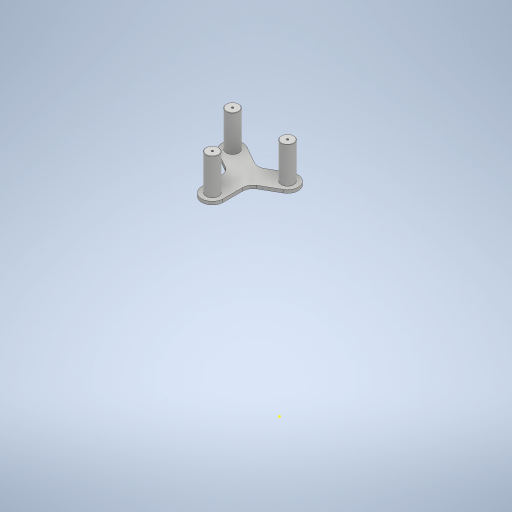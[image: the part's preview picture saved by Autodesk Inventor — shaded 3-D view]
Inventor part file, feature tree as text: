
AUTODESK INVENTOR PART (.ipt)
format: ipt  version: 2023 (Build 270158000, 158)  size: 315,904 bytes
history: native  units: mm
features: extrude x3, sketch x3, hole x3, plane x2, fillet x1
ambient origin geometry x8: Origin, YZ Plane, XZ Plane, XY Plane, X Axis, Y Axis, Z Axis, Center Point
bodies: 实体1 (feature_tree)
feature tree (12):
  plane  "工作平面5"
  extrude  "拉伸1"  Depth=12.0mm
  plane  "工作平面2"
  sketch  "草图9"  dims[d37=20.0mm d38=20.0mm]
  extrude  "拉伸3"  Depth=20.0mm
  hole  "孔4"  [1 undecoded]
  hole  "孔5"  [1 undecoded]
  hole  "孔6"  [1 undecoded]
  fillet  "圆角4"  Radius=37.0mm
  extrude  "拉伸4"  Depth=10.0mm
  sketch  "草图5"  dims[d31=12.0mm d33=12.0mm]
  sketch  "草图10"  dims[d39=15.0mm d44=10.0mm d45=3.0mm d46=0.0mm d87=12.0mm d88=37.0mm d91=0.0mm d101=10.0mm d102=10.0mm d94=1.941mm d95=5.029mm d96=4.0mm d97=2.0mm d98=90.0deg d99=10.0mm d100=20.594885mm d103=10.0mm d104=10.0mm d105=1.941mm d106=5.029mm d107=4.0mm d108=2.0mm d109=90.0deg d110=10.0mm d111=20.594885mm d112=10.0mm d113=10.0mm d114=1.941mm d115=5.029mm d116=4.0mm d117=2.0mm d118=90.0deg d119=10.0mm d120=20.594885mm d121=0.3mm d122=1.0mm d123=0.0mm]
note: 3 required parameter values undecoded (feature->parameter linkage not recoverable at this tier; creation-order binding heuristic only, values carry confidence <= 0.55)
